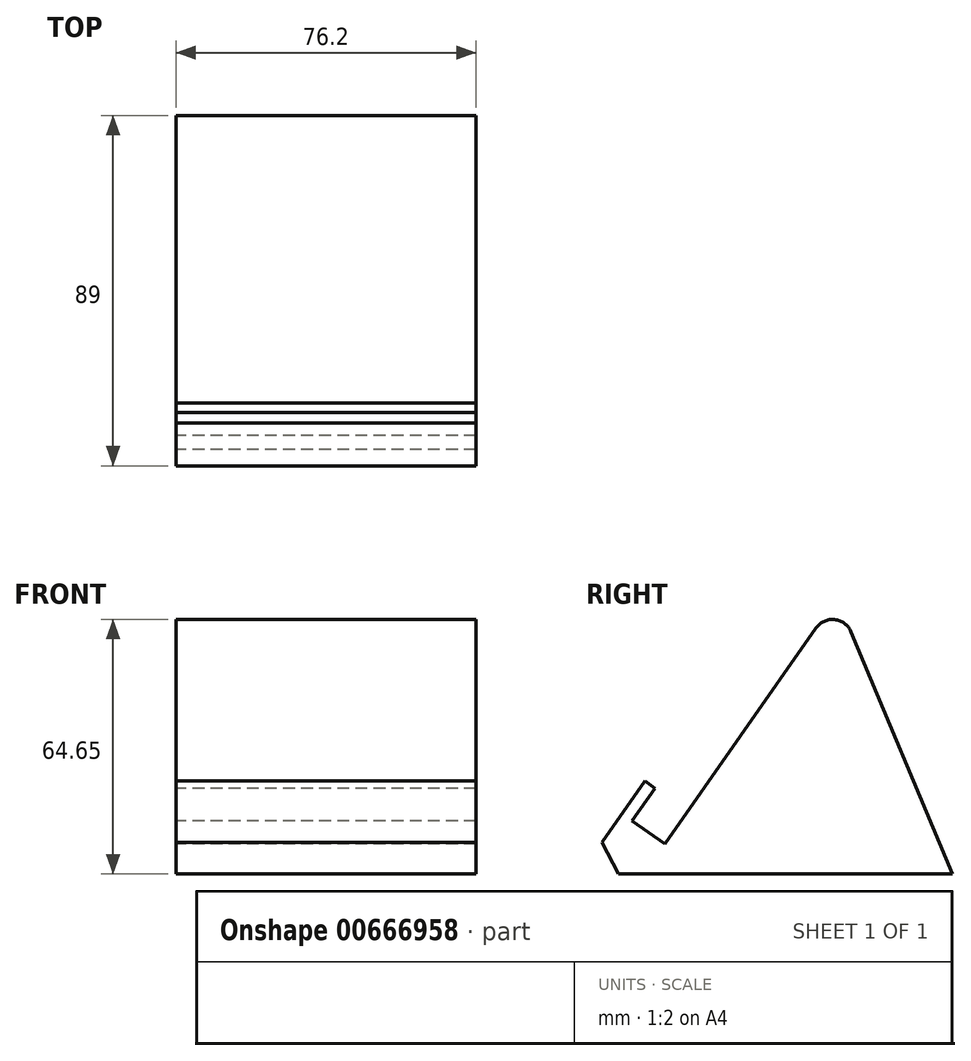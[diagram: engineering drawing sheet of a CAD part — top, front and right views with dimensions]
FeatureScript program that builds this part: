
annotation { "Feature Type Name" : "Feature", "Feature Type Description" : "" }
export const myFeature = defineFeature(function(context is Context, id is Id, definition is map)
    precondition{}
    {
        {
            var Q0;
            Q0=qCreatedBy(makeId("Right.planeOp"),FACE);
            var sketch = newSketch(context, id + "F0", { "sketchPlane" : qUnion([Q0])});
            skLineSegment(sketch, "E0", {"start": v(0, 0) * mm, "end": v(43.7, 62.42) * mm});
            skLineSegment(sketch, "E1", {"start": v(43.7, 62.42) * mm, "end": v(72.98, -7.62) * mm});
            skLineSegment(sketch, "E2", {"start": v(72.98, -7.62) * mm, "end": v(-21.61, -7.62) * mm});
            skLineSegment(sketch, "E3", {"start": v(-21.61, -7.62) * mm, "end": v(-5.1, 15.97) * mm});
            skLineSegment(sketch, "E4", {"start": v(-5.1, 15.97) * mm, "end": v(-2.5, 14.15) * mm});
            skLineSegment(sketch, "E5", {"start": v(-2.5, 14.15) * mm, "end": v(-8.32, 5.83) * mm});
            skLineSegment(sketch, "E6", {"start": v(-8.32, 5.83) * mm, "end": v(0, 0) * mm});
            skSolve(sketch);
        }
        {
            var Q0;
            Q0 = qSketchRegion(id + "F0", true);
            extrude(context, id + "F1", {"entities" : qUnion([Q0]), "endBound" : BoundingType.SYMMETRIC, "depth" : 76.2 * mm, "offsetDistance" : 25.4 * mm});
        }
        {
            var Q0;
            Q0=makeQuery(id+"F1.opExtrude","SWEPT_EDGE",EDGE,{"disambiguationData":[OSD([sQuery(id+"F0.wireOp",EDGE,"E0"),sQuery(id+"F0.wireOp",EDGE,"E1")])]});
            fillet(context, id + "F2", {"entities" : qUnion([Q0]), "radius" : 5.08 * mm, "tangentPropagation" : true, "allowEdgeOverflow" : false});
        }
        {
            var Q0;
            Q0=makeQuery(id+"F1.opExtrude","SWEPT_EDGE",EDGE,{"disambiguationData":[OSD([sQuery(id+"F0.wireOp",EDGE,"E2"),sQuery(id+"F0.wireOp",EDGE,"E3")])]});
            chamfer(context, id + "F3", {"entities" : qUnion([Q0]), "width" : 5.08 * mm, "tangentPropagation" : true});
        }
    });
